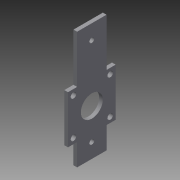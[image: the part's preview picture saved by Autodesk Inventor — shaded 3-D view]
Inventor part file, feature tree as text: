
AUTODESK INVENTOR PART (.ipt)
format: ipt  version: 2014 (Build 180170000, 170)  size: 110,592 bytes
history: native  units: in
note: dims shown in document units (in); Inventor stores cm internally (conversion verified against a paired STEP export)
features: extrude x1, sketch x1
ambient origin geometry x8: Origin, YZ Plane, XZ Plane, XY Plane, X Axis, Y Axis, Z Axis, Center Point
bodies: Solid1 (feature_tree)
feature tree (2):
  extrude  "Extrusion1"  Depth=4.0in
  sketch  "Sketch1"  dims[d0=1.0in d1=4.0in d2=1.625in d3=1.625in d5=0.164in d6=0.164in d7=1.25in d8=1.25in d10=0.1875in d11=0.5in d12=0.5in d13=0.5in d15=0.188in d16=0.7874in d18=1.25in d19=0.7874in d21=1.25in d24=0.75in d25=0.8125in d26=0.8125in d27=0.125in d28=0.0in d29=2.44in d30=0.1875in d31=0.5in]
